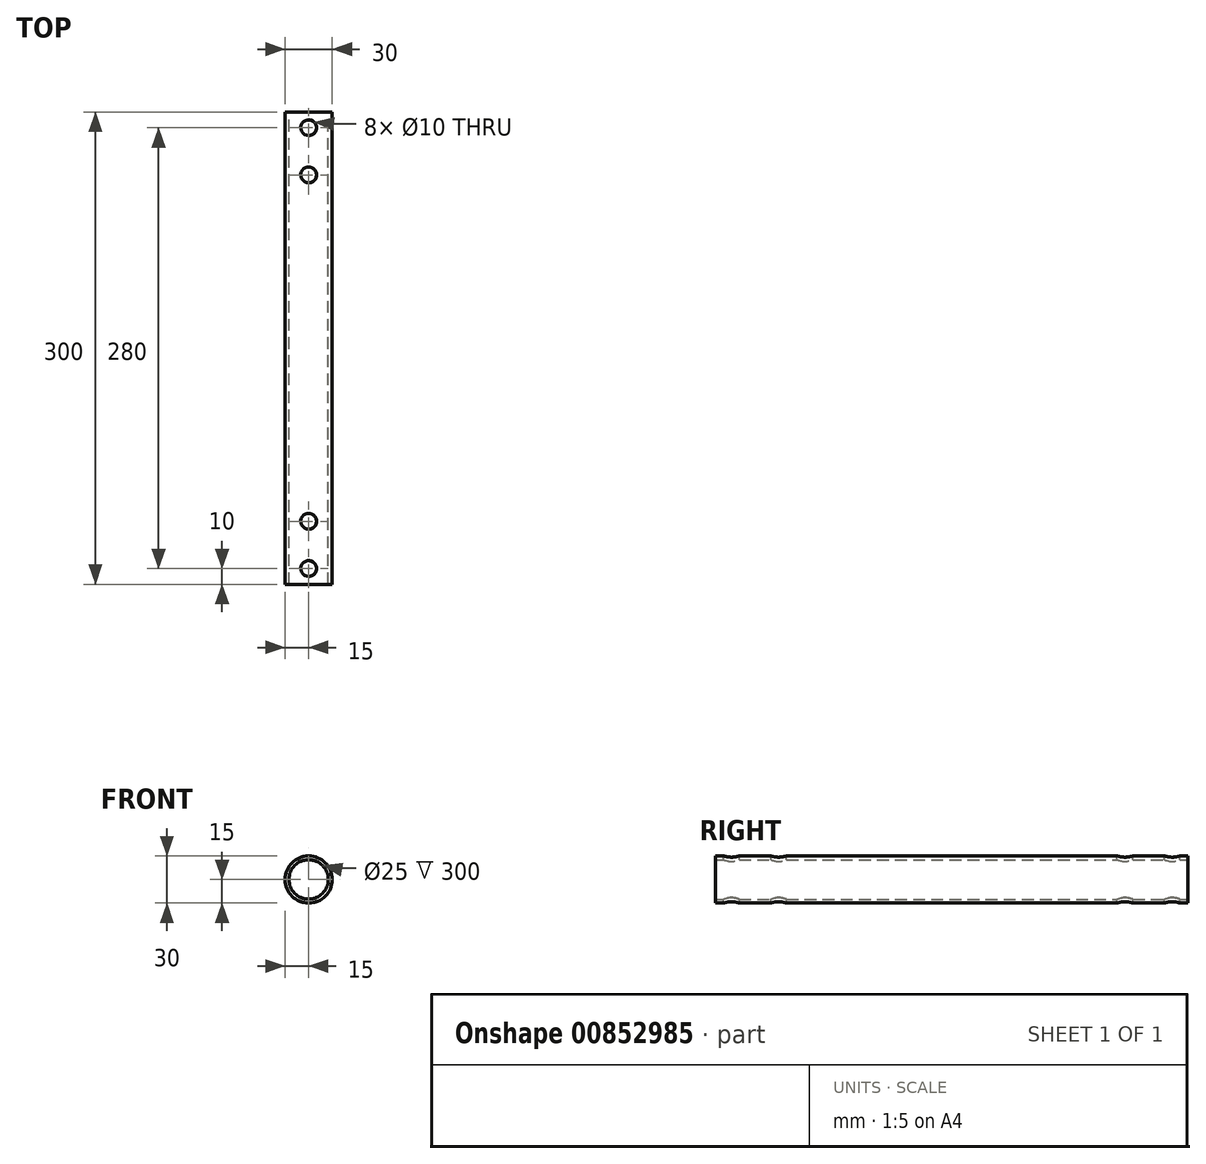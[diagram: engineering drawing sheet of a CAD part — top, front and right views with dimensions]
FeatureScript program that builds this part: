
annotation { "Feature Type Name" : "Feature", "Feature Type Description" : "" }
export const myFeature = defineFeature(function(context is Context, id is Id, definition is map)
    precondition{}
    {
        {
            var Q0;
            Q0=qCreatedBy(makeId("Front.planeOp"),FACE);
            var sketch = newSketch(context, id + "F0", { "sketchPlane" : qUnion([Q0])});
            skCircle(sketch, "E0", {"center": v(0, 0) * mm, "radius": 12.5 * mm});
            skCircle(sketch, "E1", {"center": v(0, 0) * mm, "radius": 15 * mm});
            skSolve(sketch);
        }
        {
            var Q0;
            Q0=makeQuery(id+"F0.imprint","IMPRINT",FACE,{"disambiguationData":[TD([[makeQuery(id+"F0.imprint","IMPRINT",EDGE,{"derivedFrom":sQuery(id+"F0.wireOp",EDGE,"E0")}),-1.0]])]});
            extrude(context, id + "F1", {"entities" : qUnion([Q0]), "depth" : 300 * mm, "offsetDistance" : 25 * mm});
        }
        {
            var Q0;
            Q0=qCreatedBy(makeId("Top.planeOp"),FACE);
            var sketch = newSketch(context, id + "F2", { "sketchPlane" : qUnion([Q0])});
            skLineSegment(sketch, "E2", {"start": v(0, 0) * mm, "end": v(0, -290) * mm, "construction": true});
            skCircle(sketch, "E3", {"center": v(0, -290) * mm, "radius": 5 * mm});
            skLineSegment(sketch, "E4", {"start": v(0, 0) * mm, "end": v(0, -10) * mm, "construction": true});
            skCircle(sketch, "E5", {"center": v(0, -10) * mm, "radius": 5 * mm});
            skLineSegment(sketch, "E6", {"start": v(0, -10) * mm, "end": v(0, -40) * mm});
            skCircle(sketch, "E7", {"center": v(0, -40) * mm, "radius": 5 * mm});
            skCircle(sketch, "E8", {"center": v(0, -10) * mm, "radius": 15 * mm});
            skCircle(sketch, "E9", {"center": v(0, -290) * mm, "radius": 15 * mm});
            skLineSegment(sketch, "E10", {"start": v(0, -290) * mm, "end": v(0, -260) * mm, "construction": true});
            skCircle(sketch, "E11", {"center": v(0, -260) * mm, "radius": 5 * mm});
            skSolve(sketch);
        }
        {
            var Q0;
            Q0=makeQuery(id+"F2.imprint","IMPRINT",FACE,{"disambiguationData":[TD([[makeQuery(id+"F2.imprint","IMPRINT",EDGE,{"derivedFrom":sQuery(id+"F2.wireOp",EDGE,"E3")}),1.0]])]});
            var Q1;
            Q1=makeQuery(id+"F2.imprint","IMPRINT",FACE,{"disambiguationData":[TD([[makeQuery(id+"F2.imprint","IMPRINT",EDGE,{"derivedFrom":sQuery(id+"F2.wireOp",EDGE,"E5")}),1.0]])]});
            var Q2;
            Q2=makeQuery(id+"F2.imprint","IMPRINT",FACE,{"disambiguationData":[TD([[makeQuery(id+"F2.imprint","IMPRINT",EDGE,{"derivedFrom":sQuery(id+"F2.wireOp",EDGE,"E7")}),1.0]])]});
            var Q3;
            Q3=makeQuery(id+"F2.imprint","IMPRINT",FACE,{"disambiguationData":[TD([[makeQuery(id+"F2.imprint","IMPRINT",EDGE,{"derivedFrom":sQuery(id+"F2.wireOp",EDGE,"E11")}),1.0]])]});
            extrude(context, id + "F3", {"entities" : qUnion([Q0, Q1, Q2, Q3]), "operationType" : NewBodyOperationType.REMOVE, "endBound" : BoundingType.SYMMETRIC, "oppositeDirection" : true, "depth" : 98 * mm, "offsetDistance" : 25 * mm});
        }
    });
